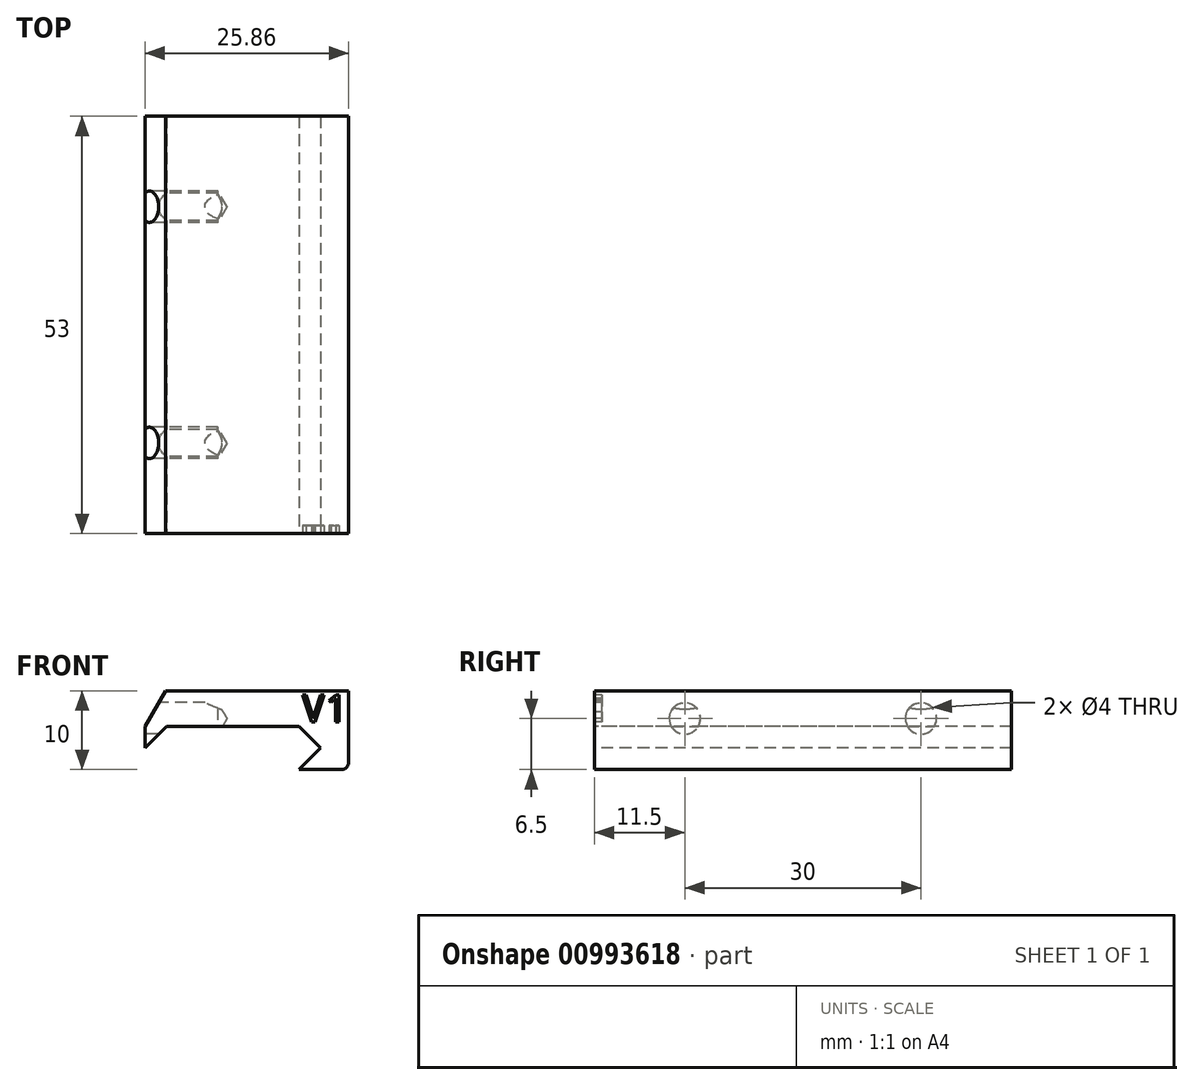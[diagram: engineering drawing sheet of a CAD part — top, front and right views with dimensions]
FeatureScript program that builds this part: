
annotation { "Feature Type Name" : "Feature", "Feature Type Description" : "" }
export const myFeature = defineFeature(function(context is Context, id is Id, definition is map)
    precondition{}
    {
        {
            var Q0;
            Q0=qCreatedBy(makeId("Front.planeOp"),FACE);
            var sketch = newSketch(context, id + "F0", { "sketchPlane" : qUnion([Q0])});
            skLineSegment(sketch, "E0.left", {"start": v(30.41, 0) * mm, "end": v(30.41, 0) * mm});
            skLineSegment(sketch, "E1.right", {"start": v(1.59, 0) * mm, "end": v(1.59, 0) * mm});
            skPoint(sketch, "E2", {"position": v(15.7, 0) * mm});
            skLineSegment(sketch, "E3", {"start": v(15.7, 0) * mm, "end": v(15.7, -20.46) * mm, "construction": true});
            skLineSegment(sketch, "E4.bottom", {"start": v(30.41, 0) * mm, "end": v(7.15, 0) * mm});
            skLineSegment(sketch, "E4.top", {"start": v(29.5, -10) * mm, "end": v(24.1, -10) * mm});
            skLineSegment(sketch, "E4.left", {"start": v(30.41, 0) * mm, "end": v(30.41, -9.08) * mm});
            skPoint(sketch, "E5", {"position": v(16, -10) * mm});
            skPoint(sketch, "E6.MirrorP", {"position": v(24.1, -10) * mm});
            skLineSegment(sketch, "E7", {"start": v(7.3, -4.5) * mm, "end": v(24.1, -4.5) * mm});
            skPoint(sketch, "E8", {"position": v(24.1, -4.5) * mm});
            skPoint(sketch, "E9", {"position": v(26.85, -7.25) * mm});
            skPoint(sketch, "E10.MirrorP", {"position": v(4.55, -7.25) * mm});
            skLineSegment(sketch, "E11", {"start": v(26.85, -7.25) * mm, "end": v(24.1, -10) * mm});
            skLineSegment(sketch, "E12", {"start": v(24.1, -4.5) * mm, "end": v(26.85, -7.25) * mm});
            skLineSegment(sketch, "E13", {"start": v(4.55, -7.25) * mm, "end": v(7.3, -4.5) * mm});
            skLineSegment(sketch, "E14", {"start": v(4.55, -7.25) * mm, "end": v(4.55, -4.5) * mm});
            skPoint(sketch, "E15.visualSharp", {"position": v(30.41, -10) * mm});
            skArc(sketch, "E15.filletArc", {"start": v(29.5, -10) * mm, "mid": v(30.14, -9.73) * mm, "end": v(30.41, -9.08) * mm});
            skPoint(sketch, "E16.end.orphan", {"position": v(7.15, 0) * mm});
            skLineSegment(sketch, "E17", {"start": v(4.55, -4.5) * mm, "end": v(7.15, 0) * mm});
            skLineSegment(sketch, "E18", {"start": v(7.15, 0) * mm, "end": v(30.41, 0) * mm});
            skText(sketch, "E19", { "text": "V1", "fontName": "DroidSansMono.ttf"});
            const initialGuessF0  = {"E19": [0.02447, -0.00396, 1, 0, 0.0035]};
            skSetInitialGuess(sketch, initialGuessF0);
            skSolve(sketch);
        }
        {
            var Q0;
            Q0=makeQuery(id+"F0.imprint","IMPRINT",FACE,{"disambiguationData":[TD([[makeQuery(id+"F0.imprint","IMPRINT",EDGE,{"derivedFrom":sQuery(id+"F0.wireOp",EDGE,"E4.top")}),-1.0]])]});
            extrude(context, id + "F1", {"entities" : qUnion([Q0]), "oppositeDirection" : true, "offsetDistance" : 25 * mm, "depth" : 53 * mm});
        }
        {
            var Q0;
            Q0=makeQuery(id+"F0.imprint","IMPRINT",FACE,{"disambiguationData":[TD([[makeQuery(id+"F0.imprint","IMPRINT",EDGE,{"derivedFrom":sQuery(id+"F0.wireOp",EDGE,"E19.sketch_text.stroke-0")}),-1.0]])]});
            var Q1;
            Q1=makeQuery(id+"F0.imprint","IMPRINT",FACE,{"disambiguationData":[TD([[makeQuery(id+"F0.imprint","IMPRINT",EDGE,{"derivedFrom":sQuery(id+"F0.wireOp",EDGE,"E19.sketch_text.stroke-9")}),-1.0]])]});
            var Q2;
            Q2=makeQuery(id+"F1.opExtrude","CAP_FACE",FACE,{"disambiguationData":[OSD([sQuery(id+"F0.wireOp",EDGE,"E4.top"),sQuery(id+"F0.wireOp",EDGE,"E4.left"),sQuery(id+"F0.wireOp",EDGE,"E7"),sQuery(id+"F0.wireOp",EDGE,"E11"),sQuery(id+"F0.wireOp",EDGE,"E12"),sQuery(id+"F0.wireOp",EDGE,"E13"),sQuery(id+"F0.wireOp",EDGE,"E14"),sQuery(id+"F0.wireOp",EDGE,"E15.filletArc"),sQuery(id+"F0.wireOp",EDGE,"E17"),sQuery(id+"F0.wireOp",EDGE,"E18"),sQuery(id+"F0.wireOp",EDGE,"E19.sketch_text.stroke-0"),sQuery(id+"F0.wireOp",EDGE,"E19.sketch_text.stroke-1"),sQuery(id+"F0.wireOp",EDGE,"E19.sketch_text.stroke-2"),sQuery(id+"F0.wireOp",EDGE,"E19.sketch_text.stroke-3"),sQuery(id+"F0.wireOp",EDGE,"E19.sketch_text.stroke-4"),sQuery(id+"F0.wireOp",EDGE,"E19.sketch_text.stroke-5"),sQuery(id+"F0.wireOp",EDGE,"E19.sketch_text.stroke-6"),sQuery(id+"F0.wireOp",EDGE,"E19.sketch_text.stroke-7"),sQuery(id+"F0.wireOp",EDGE,"E19.sketch_text.stroke-8"),sQuery(id+"F0.wireOp",EDGE,"E19.sketch_text.stroke-9"),sQuery(id+"F0.wireOp",EDGE,"E19.sketch_text.stroke-10"),sQuery(id+"F0.wireOp",EDGE,"E19.sketch_text.stroke-11"),sQuery(id+"F0.wireOp",EDGE,"E19.sketch_text.stroke-12"),sQuery(id+"F0.wireOp",EDGE,"E19.sketch_text.stroke-13"),sQuery(id+"F0.wireOp",EDGE,"E19.sketch_text.stroke-14"),sQuery(id+"F0.wireOp",EDGE,"E19.sketch_text.stroke-15"),sQuery(id+"F0.wireOp",EDGE,"E19.sketch_text.stroke-16"),sQuery(id+"F0.wireOp",EDGE,"E19.sketch_text.stroke-17")])],"isStart":false});
            extrude(context, id + "F2", {"entities" : qUnion([Q0, Q1]), "operationType" : NewBodyOperationType.ADD, "endBound" : BoundingType.UP_TO_SURFACE, "oppositeDirection" : true, "depth" : 25 * mm, "endBoundEntityFace" : qUnion([Q2]), "offsetDistance" : 25 * mm, "hasSecondDirection" : true, "secondDirectionOppositeDirection" : true, "secondDirectionDepth" : 1 * mm});
        }
        {
            var Q0;
            Q0=makeQuery(id+"F1.opExtrude","SWEPT_FACE",FACE,{"disambiguationData":[OSD([sQuery(id+"F0.wireOp",EDGE,"E14")])]});
            var sketch = newSketch(context, id + "F3", { "sketchPlane" : qUnion([Q0])});
            skSolve(sketch);
        }
        {
            var Q0;
            {var subQ0=sQuery(id+"F0.wireOp",EDGE,"E14");Q0=makeQuery(id+"F3.imprint","IMPRINT",FACE,{"disambiguationData":[TD([[makeQuery(id+"F3.imprint","IMPRINT",EDGE,{"derivedFrom":makeQuery(id+"F1.opExtrude","CAP_EDGE",EDGE,{"disambiguationData":[OSD([subQ0])],"isStart":true})}),1.0]])]});}
            var sketch = newSketch(context, id + "F4", { "sketchPlane" : qUnion([Q0])});
            skPoint(sketch, "E20", {"position": v(-26.5, -4.5) * mm});
            skPoint(sketch, "E21", {"position": v(-11.5, -3.5) * mm});
            skPoint(sketch, "E22", {"position": v(-41.5, -3.5) * mm});
            skPoint(sketch, "E23", {"position": v(-26.5, -3.5) * mm});
            skSolve(sketch);
        }
        {
            var Q0;
            Q0=sQuery(id+"F4.wireOp",VERTEX,"E21");
            var Q1;
            Q1=sQuery(id+"F4.wireOp",VERTEX,"E22");
            var Q2;
            Q2=makeQuery(id+"F1.opExtrude","SWEPT_BODY",BODY,{"disambiguationData":[OSD([sQuery(id+"F0.wireOp",EDGE,"E4.top"),sQuery(id+"F0.wireOp",EDGE,"E4.left"),sQuery(id+"F0.wireOp",EDGE,"E7"),sQuery(id+"F0.wireOp",EDGE,"E11"),sQuery(id+"F0.wireOp",EDGE,"E12"),sQuery(id+"F0.wireOp",EDGE,"E13"),sQuery(id+"F0.wireOp",EDGE,"E14"),sQuery(id+"F0.wireOp",EDGE,"E15.filletArc"),sQuery(id+"F0.wireOp",EDGE,"E17"),sQuery(id+"F0.wireOp",EDGE,"E18")])]});
            hole(context, id + "F5", {"style" : HoleStyle.SIMPLE, "endStyle" : HoleEndStyle.BLIND, "holeDiameter" : 4 * mm, "majorDiameter" : 5 * mm, "holeDepth" : 7.5 * mm, "locations" : qUnion([Q0, Q1]), "scope" : qUnion([Q2]), "tappedDepth" : 12 * mm, "tapClearance" : 3});
        }
        {
            var Q0;
            Q0=makeQuery(id+"F0.imprint","IMPRINT",FACE,{"disambiguationData":[TD([[makeQuery(id+"F0.imprint","IMPRINT",EDGE,{"derivedFrom":sQuery(id+"F0.wireOp",EDGE,"E4.top")}),-1.0]])]});
            var sketch = newSketch(context, id + "F6", { "sketchPlane" : qUnion([Q0])});
            skLineSegment(sketch, "E24.0", {"start": v(7.15, 0) * mm, "end": v(30.41, 0) * mm});
            skCircle(sketch, "E25", {"center": v(18.47, 11) * mm, "radius": 11 * mm});
            skPoint(sketch, "E25.first.point", {"position": v(18.78, 0) * mm});
            skPoint(sketch, "E25.second.point", {"position": v(18.78, 22) * mm});
            skPoint(sketch, "E25.second.point.positionSnap0", {"position": v(18.78, 0) * mm});
            skPoint(sketch, "E25.third.point", {"position": v(24.81, 19.98) * mm});
            skCircle(sketch, "E26.0", {"center": v(18.47, 11) * mm, "radius": 14 * mm});
            skLineSegment(sketch, "E27", {"start": v(18.47, 36.67) * mm, "end": v(8.52, 36.67) * mm});
            skLineSegment(sketch, "E28", {"start": v(18.47, 11) * mm, "end": v(18.47, 17.64) * mm, "construction": true});
            skLineSegment(sketch, "E29.MirrorCS", {"start": v(18.47, 36.67) * mm, "end": v(28.42, 36.67) * mm});
            skLineSegment(sketch, "E30", {"start": v(8.52, 11.18) * mm, "end": v(28.42, 11.18) * mm});
            skLineSegment(sketch, "E31", {"start": v(28.42, 11.18) * mm, "end": v(28.42, 15.68) * mm});
            skLineSegment(sketch, "E32", {"start": v(28.42, 15.68) * mm, "end": v(32.28, 13.32) * mm});
            skLineSegment(sketch, "E33", {"start": v(32.28, 13.32) * mm, "end": v(32.28, 36.67) * mm});
            skLineSegment(sketch, "E34", {"start": v(32.28, 36.67) * mm, "end": v(28.42, 36.67) * mm});
            skLineSegment(sketch, "E35.MirrorCS", {"start": v(8.52, 15.68) * mm, "end": v(4.66, 13.32) * mm});
            skLineSegment(sketch, "E36.MirrorCS", {"start": v(4.66, 13.32) * mm, "end": v(4.66, 36.67) * mm});
            skLineSegment(sketch, "E37.MirrorCS", {"start": v(4.66, 36.67) * mm, "end": v(8.52, 36.67) * mm});
            skLineSegment(sketch, "E38.trimOffspring", {"start": v(8.52, 15.68) * mm, "end": v(8.52, 11.18) * mm});
            skSolve(sketch);
        }
        {
            var Q0;
            {var subQ0=sQuery(id+"F6.wireOp",EDGE,"E26.0");var subQ1=sQuery(id+"F6.wireOp",EDGE,"E24.0");var subQ2=makeQuery(id+"F6.imprint","INTERSECT",VERTEX,{"disambiguationData":[OD(0.0)],"derivedFrom":[subQ1,subQ0]});Q0=makeQuery(id+"F6.imprint","IMPRINT",FACE,{"disambiguationData":[TD([[makeQuery(id+"F6.imprint","IMPRINT",EDGE,{"disambiguationData":[TD([[subQ2,-1.0]])],"derivedFrom":subQ1}),1.0]])]});}
            var Q1;
            {var subQ0=sQuery(id+"F6.wireOp",EDGE,"E26.0");var subQ1=sQuery(id+"F6.wireOp",EDGE,"E24.0");var subQ2=makeQuery(id+"F6.imprint","INTERSECT",VERTEX,{"disambiguationData":[OD(1.0)],"derivedFrom":[subQ1,subQ0]});Q1=makeQuery(id+"F6.imprint","IMPRINT",FACE,{"disambiguationData":[TD([[makeQuery(id+"F6.imprint","IMPRINT",EDGE,{"disambiguationData":[TD([[subQ2,1.0]])],"derivedFrom":subQ1}),1.0]])]});}
            var Q2;
            Q2=makeQuery(id+"F1.opExtrude","CAP_FACE",FACE,{"disambiguationData":[OSD([sQuery(id+"F0.wireOp",EDGE,"E4.top"),sQuery(id+"F0.wireOp",EDGE,"E4.left"),sQuery(id+"F0.wireOp",EDGE,"E7"),sQuery(id+"F0.wireOp",EDGE,"E11"),sQuery(id+"F0.wireOp",EDGE,"E12"),sQuery(id+"F0.wireOp",EDGE,"E13"),sQuery(id+"F0.wireOp",EDGE,"E14"),sQuery(id+"F0.wireOp",EDGE,"E15.filletArc"),sQuery(id+"F0.wireOp",EDGE,"E17"),sQuery(id+"F0.wireOp",EDGE,"E18")])],"isStart":false});
            extrude(context, id + "F7", {"entities" : qUnion([Q0, Q1]), "operationType" : NewBodyOperationType.ADD, "endBound" : BoundingType.UP_TO_SURFACE, "oppositeDirection" : true, "depth" : 25 * mm, "endBoundEntityFace" : qUnion([Q2]), "offsetDistance" : 25 * mm});
        }
    });
